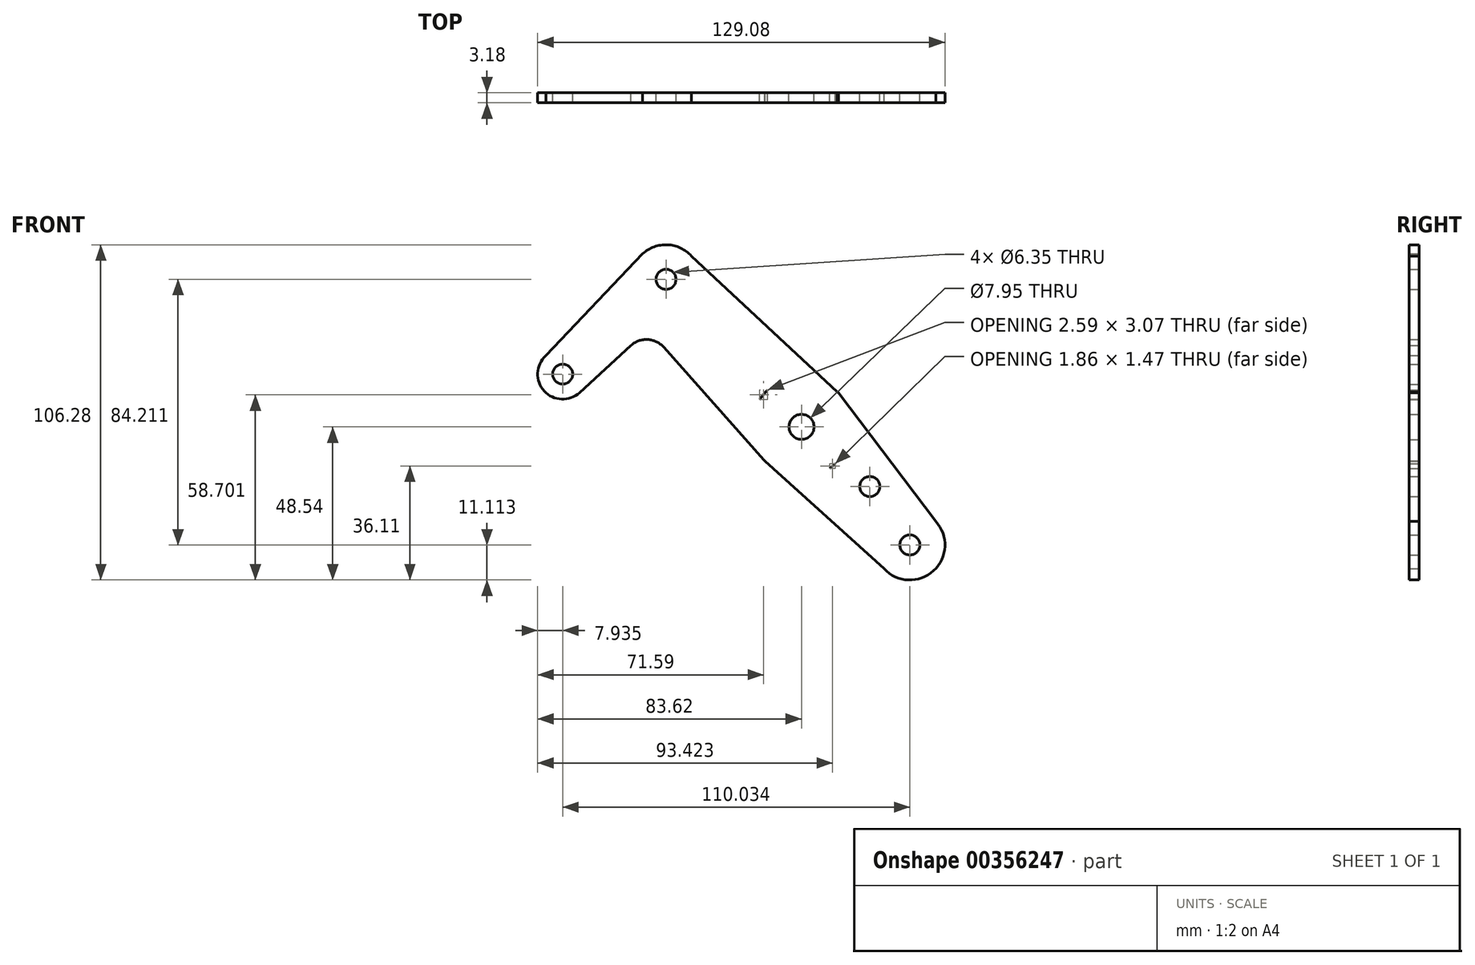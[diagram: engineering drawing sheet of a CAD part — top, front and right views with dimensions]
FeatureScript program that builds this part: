
annotation { "Feature Type Name" : "Feature", "Feature Type Description" : "" }
export const myFeature = defineFeature(function(context is Context, id is Id, definition is map)
    precondition{}
    {
        {
            var Q0;
            Q0=qCreatedBy(makeId("Front.planeOp"),FACE);
            var sketch = newSketch(context, id + "F0", { "sketchPlane" : qUnion([Q0])});
            skCircle(sketch, "E0", {"center": v(0, 0) * mm, "radius": 3.98 * mm});
            skCircle(sketch, "E1", {"center": v(0, 0) * mm, "radius": 15.88 * mm});
            skLineSegment(sketch, "E2", {"start": v(0, 0) * mm, "end": v(-42.94, 46.78) * mm});
            skLineSegment(sketch, "E3", {"start": v(-42.94, 46.78) * mm, "end": v(-75.68, 16.73) * mm});
            skCircle(sketch, "E4", {"center": v(-42.94, 46.78) * mm, "radius": 3.18 * mm});
            skCircle(sketch, "E5", {"center": v(-42.94, 46.78) * mm, "radius": 10.95 * mm});
            skCircle(sketch, "E6", {"center": v(-75.68, 16.73) * mm, "radius": 3.18 * mm});
            skCircle(sketch, "E7", {"center": v(-75.68, 16.73) * mm, "radius": 7.94 * mm});
            skLineSegment(sketch, "E8", {"start": v(0, 0) * mm, "end": v(34.35, -37.43) * mm});
            skCircle(sketch, "E9", {"center": v(0, 0) * mm, "radius": 3.18 * mm});
            skCircle(sketch, "E10", {"center": v(21.66, -18.9) * mm, "radius": 3.18 * mm});
            skLineSegment(sketch, "E11", {"start": v(0, 0) * mm, "end": v(-46.78, -42.94) * mm});
            skLineSegment(sketch, "E12", {"start": v(-46.78, -42.94) * mm, "end": v(-31.57, -28.97) * mm});
            skLineSegment(sketch, "E13", {"start": v(-46.78, -42.94) * mm, "end": v(-75.93, -11.18) * mm});
            skCircle(sketch, "E14", {"center": v(-75.93, -11.18) * mm, "radius": 7.94 * mm});
            skCircle(sketch, "E15", {"center": v(-75.93, -11.18) * mm, "radius": 3.18 * mm});
            skCircle(sketch, "E16", {"center": v(-46.78, -42.94) * mm, "radius": 11.11 * mm});
            skCircle(sketch, "E17", {"center": v(-46.78, -42.94) * mm, "radius": 3.18 * mm});
            skCircle(sketch, "E18", {"center": v(-31.57, -28.97) * mm, "radius": 3.18 * mm});
            skCircle(sketch, "E19", {"center": v(34.35, -37.43) * mm, "radius": 11.11 * mm});
            skLineSegment(sketch, "E20", {"start": v(11.49, 10.96) * mm, "end": v(11.3, 11.14) * mm});
            skLineSegment(sketch, "E21", {"start": v(11.49, 10.96) * mm, "end": v(11.66, 10.77) * mm});
            skLineSegment(sketch, "E22", {"start": v(11.3, 11.14) * mm, "end": v(-34.87, 54.19) * mm});
            skLineSegment(sketch, "E23", {"start": v(-81.05, 22.58) * mm, "end": v(-50.34, 54.85) * mm});
            skLineSegment(sketch, "E24", {"start": v(-11.7, -10.73) * mm, "end": v(-11.87, -10.55) * mm});
            skLineSegment(sketch, "E25", {"start": v(-11.7, -10.73) * mm, "end": v(-11.52, -10.92) * mm});
            skLineSegment(sketch, "E26", {"start": v(11.66, 10.77) * mm, "end": v(42.54, -29.91) * mm});
            skLineSegment(sketch, "E27", {"start": v(-11.52, -10.92) * mm, "end": v(26.16, -44.94) * mm});
            skLineSegment(sketch, "E28", {"start": v(-75.68, 16.73) * mm, "end": v(-70.32, 10.88) * mm});
            skLineSegment(sketch, "E29", {"start": v(-11.87, -10.55) * mm, "end": v(-43.7, 25.27) * mm});
            skArc(sketch, "E30", {"start": v(-43.7, 25.27) * mm, "mid": v(-48.73, 27.7) * mm, "end": v(-54, 25.85) * mm});
            skLineSegment(sketch, "E31", {"start": v(-54, 25.85) * mm, "end": v(-70.32, 10.88) * mm});
            skLineSegment(sketch, "E32", {"start": v(10.73, -11.7) * mm, "end": v(-39.36, -51.2) * mm});
            skLineSegment(sketch, "E33", {"start": v(-55.26, -50.13) * mm, "end": v(-82.16, -16.1) * mm});
            skLineSegment(sketch, "E34", {"start": v(-70.44, -5.45) * mm, "end": v(-50.38, -24.69) * mm});
            skArc(sketch, "E35", {"start": v(-50.38, -24.69) * mm, "mid": v(-45.92, -26.48) * mm, "end": v(-41.46, -24.69) * mm});
            skLineSegment(sketch, "E36", {"start": v(-10.73, 11.7) * mm, "end": v(-41.46, -24.69) * mm});
            skCircle(sketch, "E37", {"center": v(34.35, -37.43) * mm, "radius": 3.18 * mm});
            skSolve(sketch);
        }
        {
            var Q0;
            {var subQ13=sQuery(id+"F0.wireOp",EDGE,"E20");Q0=makeQuery(id+"F0.imprint","IMPRINT",FACE,{"disambiguationData":[TD([[makeQuery(id+"F0.imprint","IMPRINT",EDGE,{"derivedFrom":subQ13}),1.0]])]});}
            var Q1;
            {var subQ6=sQuery(id+"F0.wireOp",EDGE,"E24");Q1=makeQuery(id+"F0.imprint","IMPRINT",FACE,{"disambiguationData":[TD([[makeQuery(id+"F0.imprint","IMPRINT",EDGE,{"derivedFrom":subQ6}),-1.0]])]});}
            var Q2;
            {var subQ0=sQuery(id+"F0.wireOp",EDGE,"E25");Q2=makeQuery(id+"F0.imprint","IMPRINT",FACE,{"disambiguationData":[TD([[makeQuery(id+"F0.imprint","IMPRINT",EDGE,{"derivedFrom":subQ0}),1.0]])]});}
            var Q3;
            {var subQ0=sQuery(id+"F0.wireOp",EDGE,"E8");var subQ1=makeQuery(id+"F0.imprint","INTERSECT",VERTEX,{"derivedFrom":[subQ0,sQuery(id+"F0.wireOp",EDGE,"E10")]});Q3=makeQuery(id+"F0.imprint","IMPRINT",FACE,{"disambiguationData":[TD([[makeQuery(id+"F0.imprint","IMPRINT",EDGE,{"disambiguationData":[TD([[subQ1,-1.0]])],"derivedFrom":subQ0}),-1.0]])]});}
            var Q4;
            {var subQ0=sQuery(id+"F0.wireOp",EDGE,"E27");var subQ1=sQuery(id+"F0.wireOp",EDGE,"E1");var subQ2=makeQuery(id+"F0.imprint","INTERSECT",VERTEX,{"derivedFrom":[subQ1,subQ0]});Q4=makeQuery(id+"F0.imprint","IMPRINT",FACE,{"disambiguationData":[TD([[makeQuery(id+"F0.imprint","IMPRINT",EDGE,{"disambiguationData":[TD([[subQ2,-1.0]])],"derivedFrom":subQ1}),-1.0]])]});}
            var Q5;
            {var subQ0=sQuery(id+"F0.wireOp",EDGE,"E10");Q5=makeQuery(id+"F0.imprint","IMPRINT",FACE,{"disambiguationData":[TD([[makeQuery(id+"F0.imprint","IMPRINT",EDGE,{"derivedFrom":subQ0}),-1.0]])]});}
            var Q6;
            Q6=makeQuery(id+"F0.imprint","IMPRINT",FACE,{"disambiguationData":[TD([[makeQuery(id+"F0.imprint","IMPRINT",EDGE,{"derivedFrom":sQuery(id+"F0.wireOp",EDGE,"E37")}),-1.0]])]});
            var Q7;
            {var subQ0=sQuery(id+"F0.wireOp",EDGE,"E29");var subQ3=sQuery(id+"F0.wireOp",EDGE,"E36");var subQ5=makeQuery(id+"F0.imprint","INTERSECT",VERTEX,{"derivedFrom":[subQ0,subQ3]});Q7=makeQuery(id+"F0.imprint","IMPRINT",FACE,{"disambiguationData":[TD([[makeQuery(id+"F0.imprint","IMPRINT",EDGE,{"disambiguationData":[TD([[subQ5,1.0]])],"derivedFrom":subQ3}),1.0]])]});}
            var Q8;
            {var subQ12=sQuery(id+"F0.wireOp",EDGE,"E30");Q8=makeQuery(id+"F0.imprint","IMPRINT",FACE,{"disambiguationData":[TD([[makeQuery(id+"F0.imprint","IMPRINT",EDGE,{"derivedFrom":subQ12}),-1.0]])]});}
            var Q9;
            {var subQ3=sQuery(id+"F0.wireOp",EDGE,"E22");var subQ5=sQuery(id+"F0.wireOp",EDGE,"E5");var subQ7=makeQuery(id+"F0.imprint","INTERSECT",VERTEX,{"derivedFrom":[subQ5,subQ3]});Q9=makeQuery(id+"F0.imprint","IMPRINT",FACE,{"disambiguationData":[TD([[makeQuery(id+"F0.imprint","IMPRINT",EDGE,{"disambiguationData":[TD([[subQ7,1.0]])],"derivedFrom":subQ5}),-1.0]])]});}
            var Q10;
            {var subQ0=sQuery(id+"F0.wireOp",EDGE,"E5");var subQ1=sQuery(id+"F0.wireOp",EDGE,"E2");var subQ2=makeQuery(id+"F0.imprint","INTERSECT",VERTEX,{"derivedFrom":[subQ1,subQ0]});Q10=makeQuery(id+"F0.imprint","IMPRINT",FACE,{"disambiguationData":[TD([[makeQuery(id+"F0.imprint","IMPRINT",EDGE,{"disambiguationData":[TD([[subQ2,-1.0]])],"derivedFrom":subQ1}),1.0]])]});}
            var Q11;
            {var subQ0=sQuery(id+"F0.wireOp",EDGE,"E5");var subQ5=sQuery(id+"F0.wireOp",EDGE,"E2");var subQ10=makeQuery(id+"F0.imprint","INTERSECT",VERTEX,{"derivedFrom":[subQ5,subQ0]});Q11=makeQuery(id+"F0.imprint","IMPRINT",FACE,{"disambiguationData":[TD([[makeQuery(id+"F0.imprint","IMPRINT",EDGE,{"disambiguationData":[TD([[subQ10,-1.0]])],"derivedFrom":subQ5}),-1.0]])]});}
            var Q12;
            {var subQ0=sQuery(id+"F0.wireOp",EDGE,"E5");var subQ1=sQuery(id+"F0.wireOp",EDGE,"E3");var subQ2=makeQuery(id+"F0.imprint","INTERSECT",VERTEX,{"derivedFrom":[subQ1,subQ0]});Q12=makeQuery(id+"F0.imprint","IMPRINT",FACE,{"disambiguationData":[TD([[makeQuery(id+"F0.imprint","IMPRINT",EDGE,{"disambiguationData":[TD([[subQ2,-1.0]])],"derivedFrom":subQ1}),-1.0]])]});}
            var Q13;
            {var subQ0=sQuery(id+"F0.wireOp",EDGE,"E7");var subQ1=sQuery(id+"F0.wireOp",EDGE,"E3");var subQ2=makeQuery(id+"F0.imprint","INTERSECT",VERTEX,{"derivedFrom":[subQ1,subQ0]});Q13=makeQuery(id+"F0.imprint","IMPRINT",FACE,{"disambiguationData":[TD([[makeQuery(id+"F0.imprint","IMPRINT",EDGE,{"disambiguationData":[TD([[subQ2,-1.0]])],"derivedFrom":subQ1}),1.0]])]});}
            var Q14;
            {var subQ0=sQuery(id+"F0.wireOp",EDGE,"E7");var subQ4=sQuery(id+"F0.wireOp",EDGE,"E3");var subQ5=makeQuery(id+"F0.imprint","INTERSECT",VERTEX,{"derivedFrom":[subQ4,subQ0]});Q14=makeQuery(id+"F0.imprint","IMPRINT",FACE,{"disambiguationData":[TD([[makeQuery(id+"F0.imprint","IMPRINT",EDGE,{"disambiguationData":[TD([[subQ5,-1.0]])],"derivedFrom":subQ4}),-1.0]])]});}
            extrude(context, id + "F1", {"entities" : qUnion([Q0, Q1, Q2, Q3, Q4, Q5, Q6, Q7, Q8, Q9, Q10, Q11, Q12, Q13, Q14]), "depth" : 3.17 * mm});
        }
    });
